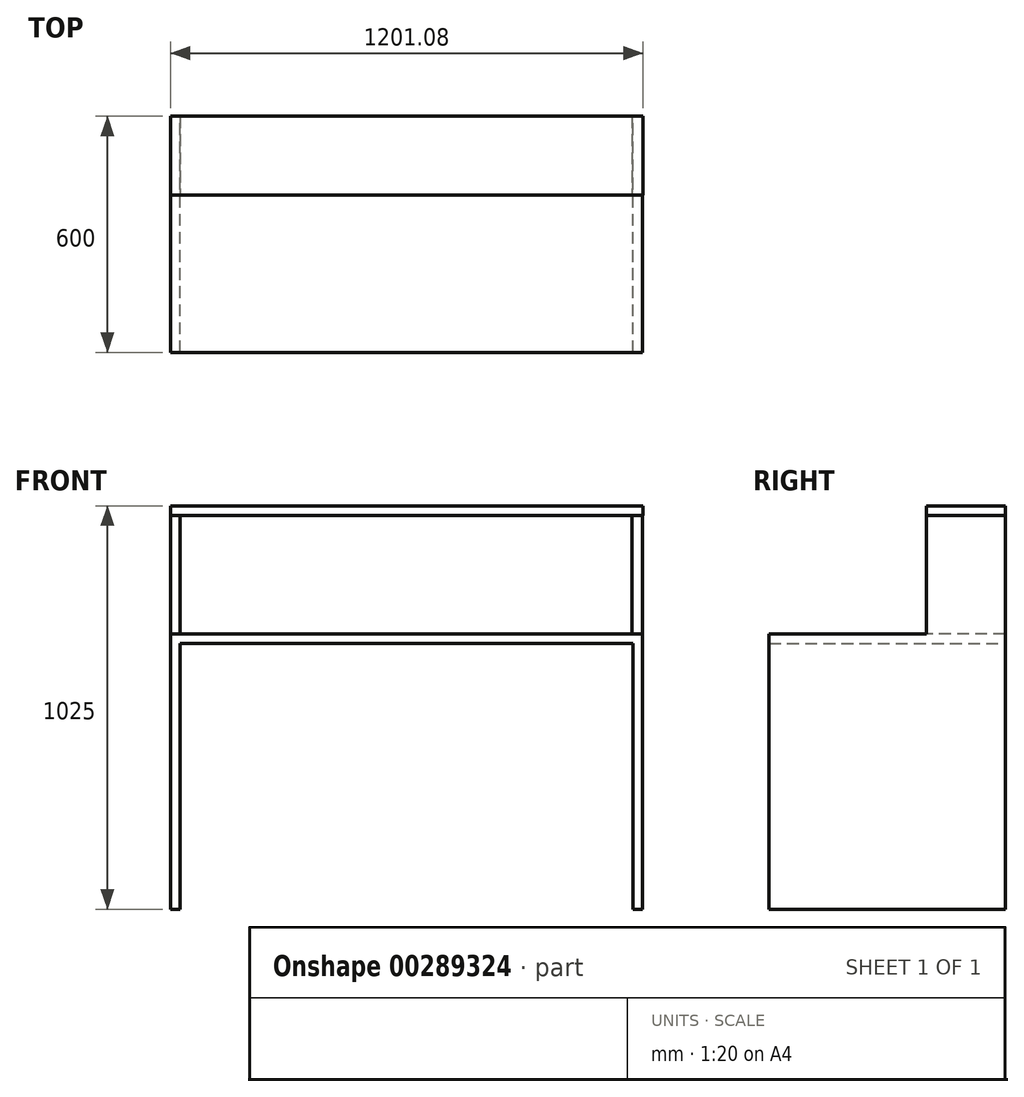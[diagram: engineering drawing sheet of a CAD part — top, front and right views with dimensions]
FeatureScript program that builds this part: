
annotation { "Feature Type Name" : "Feature", "Feature Type Description" : "" }
export const myFeature = defineFeature(function(context is Context, id is Id, definition is map)
    precondition{}
    {
        {
            var Q0;
            Q0=qCreatedBy(makeId("Top.planeOp"),FACE);
            var sketch = newSketch(context, id + "F0", { "sketchPlane" : qUnion([Q0])});
            skLineSegment(sketch, "E0.bottom", {"start": v(600, -300) * mm, "end": v(-600, -300) * mm});
            skLineSegment(sketch, "E0.top", {"start": v(600, 300) * mm, "end": v(-600, 300) * mm});
            skLineSegment(sketch, "E0.left", {"start": v(600, -300) * mm, "end": v(600, 300) * mm});
            skLineSegment(sketch, "E0.right", {"start": v(-600, -300) * mm, "end": v(-600, 300) * mm});
            skPoint(sketch, "E0.middle", {"position": v(0, 0) * mm});
            skSolve(sketch);
        }
        {
            var Q0;
            Q0 = qSketchRegion(id + "F0", true);
            extrude(context, id + "F1", {"entities" : qUnion([Q0]), "depth" : 25 * mm});
        }
        {
            var Q0;
            Q0=makeQuery(id+"F1.opExtrude","CAP_FACE",FACE,{"disambiguationData":[OSD([sQuery(id+"F0.wireOp",EDGE,"E0.bottom"),sQuery(id+"F0.wireOp",EDGE,"E0.top"),sQuery(id+"F0.wireOp",EDGE,"E0.left"),sQuery(id+"F0.wireOp",EDGE,"E0.right")])],"isStart":true});
            var sketch = newSketch(context, id + "F2", { "sketchPlane" : qUnion([Q0])});
            skLineSegment(sketch, "E1.bottom", {"start": v(-575, 300) * mm, "end": v(575, 300) * mm});
            skLineSegment(sketch, "E1.top", {"start": v(-575, -300) * mm, "end": v(575, -300) * mm});
            skLineSegment(sketch, "E1.left", {"start": v(-575, 300) * mm, "end": v(-575, -300) * mm});
            skLineSegment(sketch, "E1.right", {"start": v(575, 300) * mm, "end": v(575, -300) * mm});
            skSolve(sketch);
        }
        {
            var Q0;
            {var subQ0=sQuery(id+"F2.wireOp",EDGE,"E1.left");Q0=makeQuery(id+"F2.imprint","IMPRINT",FACE,{"disambiguationData":[TD([[makeQuery(id+"F2.imprint","IMPRINT",EDGE,{"derivedFrom":subQ0}),-1.0]])]});}
            var Q1;
            {var subQ0=sQuery(id+"F2.wireOp",EDGE,"E1.right");Q1=makeQuery(id+"F2.imprint","IMPRINT",FACE,{"disambiguationData":[TD([[makeQuery(id+"F2.imprint","IMPRINT",EDGE,{"derivedFrom":subQ0}),1.0]])]});}
            extrude(context, id + "F3", {"entities" : qUnion([Q0, Q1]), "operationType" : NewBodyOperationType.ADD, "depth" : 675 * mm});
        }
        {
            var Q0;
            Q0=makeQuery(id+"F1.opExtrude","CAP_FACE",FACE,{"disambiguationData":[OSD([sQuery(id+"F0.wireOp",EDGE,"E0.bottom"),sQuery(id+"F0.wireOp",EDGE,"E0.top"),sQuery(id+"F0.wireOp",EDGE,"E0.left"),sQuery(id+"F0.wireOp",EDGE,"E0.right")])],"isStart":false});
            var sketch = newSketch(context, id + "F4", { "sketchPlane" : qUnion([Q0])});
            skLineSegment(sketch, "E2.bottom", {"start": v(-575.26, 300) * mm, "end": v(573.2, 300) * mm});
            skLineSegment(sketch, "E2.top", {"start": v(-575.26, -300) * mm, "end": v(573.2, -300) * mm});
            skLineSegment(sketch, "E2.left", {"start": v(-575.26, 300) * mm, "end": v(-575.26, -300) * mm});
            skLineSegment(sketch, "E2.right", {"start": v(573.2, 300) * mm, "end": v(573.2, -300) * mm});
            skLineSegment(sketch, "E3", {"start": v(-600, 100) * mm, "end": v(-575.26, 100) * mm});
            skLineSegment(sketch, "E4", {"start": v(-575.26, 100) * mm, "end": v(600, 100) * mm});
            skSolve(sketch);
        }
        {
            var Q0;
            {var subQ3=sQuery(id+"F4.wireOp",EDGE,"E3");Q0=makeQuery(id+"F4.imprint","IMPRINT",FACE,{"disambiguationData":[TD([[makeQuery(id+"F4.imprint","IMPRINT",EDGE,{"derivedFrom":subQ3}),1.0]])]});}
            var Q1;
            {var subQ3=sQuery(id+"F4.wireOp",EDGE,"E4");var subQ5=makeQuery(id+"F1.opExtrude","CAP_EDGE",EDGE,{"disambiguationData":[OSD([sQuery(id+"F0.wireOp",EDGE,"E0.left")])],"isStart":false});var subQ7=makeQuery(id+"F4.imprint","INTERSECT",VERTEX,{"derivedFrom":[subQ5,subQ3]});Q1=makeQuery(id+"F4.imprint","IMPRINT",FACE,{"disambiguationData":[TD([[makeQuery(id+"F4.imprint","IMPRINT",EDGE,{"disambiguationData":[TD([[subQ7,1.0]])],"derivedFrom":subQ3}),1.0]])]});}
            extrude(context, id + "F5", {"entities" : qUnion([Q0, Q1]), "operationType" : NewBodyOperationType.ADD, "depth" : 300 * mm});
        }
        {
            var Q0;
            Q0=makeQuery(id+"F5.opExtrude","CAP_FACE",FACE,{"disambiguationData":[OSD([sQuery(id+"F0.wireOp",EDGE,"E0.top"),sQuery(id+"F0.wireOp",EDGE,"E0.right"),sQuery(id+"F4.wireOp",EDGE,"E2.left"),sQuery(id+"F4.wireOp",EDGE,"E3")])],"isStart":false});
            var sketch = newSketch(context, id + "F6", { "sketchPlane" : qUnion([Q0])});
            skLineSegment(sketch, "E5.bottom", {"start": v(-600, 300) * mm, "end": v(601.08, 300) * mm});
            skLineSegment(sketch, "E5.top", {"start": v(-600, 99.66) * mm, "end": v(601.08, 99.66) * mm});
            skLineSegment(sketch, "E5.left", {"start": v(-600, 300) * mm, "end": v(-600, 99.66) * mm});
            skLineSegment(sketch, "E5.right", {"start": v(601.08, 300) * mm, "end": v(601.08, 99.66) * mm});
            skSolve(sketch);
        }
        {
            var Q0;
            {var subQ3=makeQuery(id+"F5.opExtrude","CAP_EDGE",EDGE,{"disambiguationData":[OSD([sQuery(id+"F4.wireOp",EDGE,"E2.left")])],"isStart":false});Q0=makeQuery(id+"F6.imprint","IMPRINT",FACE,{"disambiguationData":[TD([[makeQuery(id+"F6.imprint","IMPRINT",EDGE,{"derivedFrom":subQ3}),-1.0]])]});}
            var Q1;
            {var subQ2=sQuery(id+"F6.wireOp",EDGE,"E5.top");Q1=makeQuery(id+"F6.imprint","IMPRINT",FACE,{"disambiguationData":[TD([[makeQuery(id+"F6.imprint","IMPRINT",EDGE,{"derivedFrom":subQ2}),1.0]])]});}
            extrude(context, id + "F7", {"entities" : qUnion([Q0, Q1]), "operationType" : NewBodyOperationType.ADD, "depth" : 25 * mm});
        }
    });
